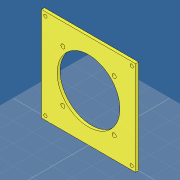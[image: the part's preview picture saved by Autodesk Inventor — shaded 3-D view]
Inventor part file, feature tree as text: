
AUTODESK INVENTOR PART (.ipt)
format: ipt  version: 2019 (Build 230136000, 136)  size: 109,056 bytes
history: native  units: mm
features: hole x2, sketch x1, extrude x1
ambient origin geometry x8: Origin, YZ Plane, XZ Plane, XY Plane, X Axis, Y Axis, Z Axis, Center Point
bodies: Volumenkörper1 (feature_tree)
feature tree (4):
  sketch  "Skizze1"  dims[d0=96.0mm d1=96.0mm d27=3.0mm d28=0.0mm d41=64.0mm d42=74.0mm d43=8.0mm d44=8.0mm d45=3.4mm d46=6.0mm d47=4.0mm d48=2.0mm d49=90.0deg d50=8.0mm d51=20.594885mm d52=4.2mm d53=6.0mm d54=4.0mm d55=2.0mm d56=90.0deg d57=8.0mm d58=20.594885mm]
  extrude  "Extrusion1"  Depth=96.0mm
  hole  "Bohrung2"  [1 undecoded]
  hole  "Bohrung3"  [1 undecoded]
note: 2 required parameter values undecoded (feature->parameter linkage not recoverable at this tier; creation-order binding heuristic only, values carry confidence <= 0.55)
